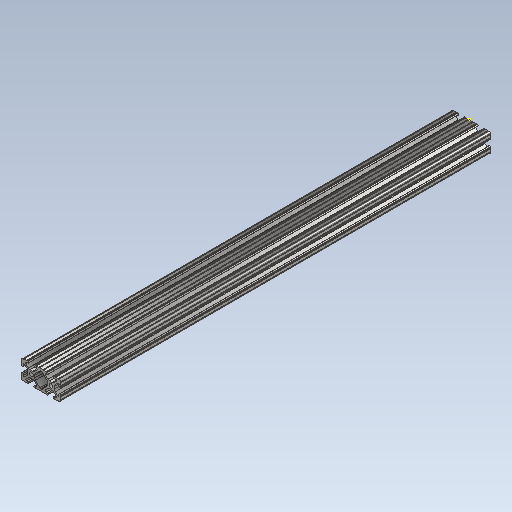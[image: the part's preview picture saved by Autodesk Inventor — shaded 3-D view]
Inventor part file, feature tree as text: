
AUTODESK INVENTOR PART (.ipt)
format: ipt  version: 2020 (Build 240168000, 168)  size: 343,040 bytes
history: native  units: in
note: dims shown in document units (in); Inventor stores cm internally (conversion verified against a paired STEP export)
features: sketch x2, extrude x1
ambient origin geometry x8: Origin, YZ Plane, XZ Plane, XY Plane, X Axis, Y Axis, Z Axis, Center Point
bodies: Solid1 (feature_tree)
feature tree (3):
  extrude  "Extrusion1"  [1 undecoded]
  sketch  "Sketch2"
  sketch  "Sketch1"  dims[d0=22.0in d1=0.0in]
note: 1 required parameter value undecoded (feature->parameter linkage not recoverable at this tier; creation-order binding heuristic only, values carry confidence <= 0.55)
